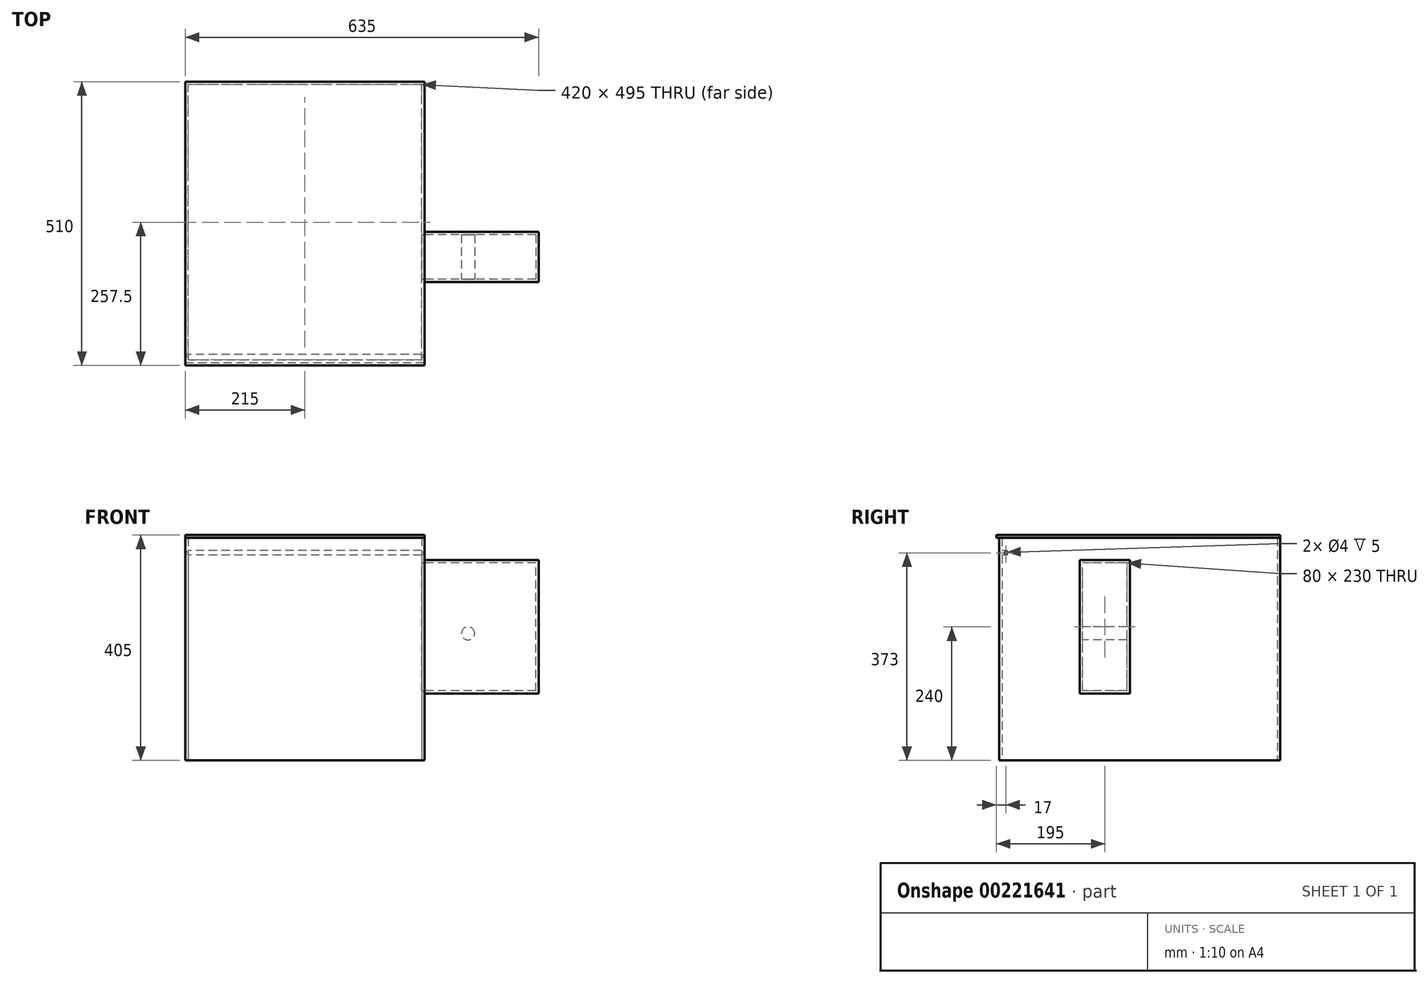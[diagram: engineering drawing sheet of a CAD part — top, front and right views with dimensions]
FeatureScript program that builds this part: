
annotation { "Feature Type Name" : "Feature", "Feature Type Description" : "" }
export const myFeature = defineFeature(function(context is Context, id is Id, definition is map)
    precondition{}
    {
        {
            var Q0;
            Q0=qCreatedBy(makeId("Top.planeOp"),FACE);
            var sketch = newSketch(context, id + "F0", { "sketchPlane" : qUnion([Q0])});
            skLineSegment(sketch, "E0.bottom", {"start": v(210, -250) * mm, "end": v(-210, -250) * mm});
            skLineSegment(sketch, "E0.top", {"start": v(210, 250) * mm, "end": v(-210, 250) * mm});
            skLineSegment(sketch, "E0.left", {"start": v(210, -250) * mm, "end": v(210, 250) * mm});
            skLineSegment(sketch, "E0.right", {"start": v(-210, -250) * mm, "end": v(-210, 250) * mm});
            skPoint(sketch, "E0.middle", {"position": v(0, 0) * mm});
            skLineSegment(sketch, "E1.0", {"start": v(-215, -250) * mm, "end": v(-215, 255) * mm});
            skLineSegment(sketch, "E1.1", {"start": v(215, 255) * mm, "end": v(-215, 255) * mm});
            skLineSegment(sketch, "E1.2", {"start": v(215, -250) * mm, "end": v(215, 255) * mm});
            skLineSegment(sketch, "E2", {"start": v(-215, -250) * mm, "end": v(-210, -250) * mm});
            skLineSegment(sketch, "E3", {"start": v(210, -250) * mm, "end": v(215, -250) * mm});
            skLineSegment(sketch, "E4", {"start": v(-210, -245) * mm, "end": v(210, -245) * mm});
            skSolve(sketch);
        }
        {
            var Q0;
            Q0=makeQuery(id+"F0.imprint","IMPRINT",FACE,{"disambiguationData":[TD([[makeQuery(id+"F0.imprint","IMPRINT",EDGE,{"derivedFrom":sQuery(id+"F0.wireOp",EDGE,"E0.top")}),-1.0]])]});
            extrude(context, id + "F1", {"entities" : qUnion([Q0]), "depth" : 400 * mm});
        }
        {
            var Q0;
            Q0=makeQuery(id+"F1.opExtrude","CAP_FACE",FACE,{"disambiguationData":[OSD([sQuery(id+"F0.wireOp",EDGE,"E0.top"),sQuery(id+"F0.wireOp",EDGE,"E0.left"),sQuery(id+"F0.wireOp",EDGE,"E0.right"),sQuery(id+"F0.wireOp",EDGE,"E1.0"),sQuery(id+"F0.wireOp",EDGE,"E1.1"),sQuery(id+"F0.wireOp",EDGE,"E1.2"),sQuery(id+"F0.wireOp",EDGE,"E2"),sQuery(id+"F0.wireOp",EDGE,"E3")])],"isStart":false});
            var sketch = newSketch(context, id + "F2", { "sketchPlane" : qUnion([Q0])});
            skLineSegment(sketch, "E5.bottom", {"start": v(215, 255) * mm, "end": v(-215, 255) * mm});
            skLineSegment(sketch, "E5.top", {"start": v(215, -255) * mm, "end": v(-215, -255) * mm});
            skLineSegment(sketch, "E5.left", {"start": v(215, 255) * mm, "end": v(215, -255) * mm});
            skLineSegment(sketch, "E5.right", {"start": v(-215, 255) * mm, "end": v(-215, -255) * mm});
            skPoint(sketch, "E5.middle", {"position": v(0, 0) * mm});
            skSolve(sketch);
        }
        {
            var Q0;
            {var subQ2=sQuery(id+"F2.wireOp",EDGE,"E5.top");Q0=makeQuery(id+"F2.imprint","IMPRINT",FACE,{"disambiguationData":[TD([[makeQuery(id+"F2.imprint","IMPRINT",EDGE,{"derivedFrom":subQ2}),-1.0]])]});}
            var Q1;
            {var subQ2=sQuery(id+"F2.wireOp",EDGE,"E5.bottom");Q1=makeQuery(id+"F2.imprint","IMPRINT",FACE,{"disambiguationData":[TD([[makeQuery(id+"F2.imprint","IMPRINT",EDGE,{"derivedFrom":subQ2}),1.0]])]});}
            extrude(context, id + "F3", {"entities" : qUnion([Q0, Q1]), "depth" : 5 * mm});
        }
        {
            var Q0;
            Q0=makeQuery(id+"F1.opExtrude","SWEPT_FACE",FACE,{"disambiguationData":[OSD([sQuery(id+"F0.wireOp",EDGE,"E1.0")])]});
            var sketch = newSketch(context, id + "F4", { "sketchPlane" : qUnion([Q0])});
            skCircle(sketch, "E6", {"center": v(238, 373) * mm, "radius": 2 * mm});
            skSolve(sketch);
        }
        {
            var Q0;
            Q0=makeQuery(id+"F4.imprint","IMPRINT",FACE,{"disambiguationData":[TD([[makeQuery(id+"F4.imprint","IMPRINT",EDGE,{"derivedFrom":sQuery(id+"F4.wireOp",EDGE,"E6")}),1.0]])]});
            extrude(context, id + "F5", {"entities" : qUnion([Q0]), "operationType" : NewBodyOperationType.REMOVE, "endBound" : BoundingType.UP_TO_NEXT, "oppositeDirection" : true, "depth" : 25 * mm});
        }
        {
            var Q0;
            Q0=makeQuery(id+"F1.opExtrude","SWEPT_FACE",FACE,{"disambiguationData":[OSD([sQuery(id+"F0.wireOp",EDGE,"E1.2")])]});
            var sketch = newSketch(context, id + "F6", { "sketchPlane" : qUnion([Q0])});
            skCircle(sketch, "E7", {"center": v(-238, 373) * mm, "radius": 2 * mm});
            skLineSegment(sketch, "E8.bottom", {"start": v(-20, 125) * mm, "end": v(-100, 125) * mm});
            skLineSegment(sketch, "E8.top", {"start": v(-20, 355) * mm, "end": v(-100, 355) * mm});
            skLineSegment(sketch, "E8.left", {"start": v(-20, 125) * mm, "end": v(-20, 355) * mm});
            skLineSegment(sketch, "E8.right", {"start": v(-100, 125) * mm, "end": v(-100, 355) * mm});
            skPoint(sketch, "E8.middle", {"position": v(-60, 240) * mm});
            skLineSegment(sketch, "E9.0", {"start": v(-105, 120) * mm, "end": v(-105, 360) * mm});
            skLineSegment(sketch, "E9.1", {"start": v(-15, 120) * mm, "end": v(-105, 120) * mm});
            skLineSegment(sketch, "E9.2", {"start": v(-15, 120) * mm, "end": v(-15, 360) * mm});
            skLineSegment(sketch, "E9.3", {"start": v(-15, 360) * mm, "end": v(-105, 360) * mm});
            skSolve(sketch);
        }
        {
            var Q0;
            Q0=makeQuery(id+"F6.imprint","IMPRINT",FACE,{"disambiguationData":[TD([[makeQuery(id+"F6.imprint","IMPRINT",EDGE,{"derivedFrom":sQuery(id+"F6.wireOp",EDGE,"E7")}),1.0]])]});
            extrude(context, id + "F7", {"entities" : qUnion([Q0]), "operationType" : NewBodyOperationType.REMOVE, "endBound" : BoundingType.UP_TO_NEXT, "oppositeDirection" : true, "depth" : 25 * mm});
        }
        {
            var Q0;
            Q0=makeQuery(id+"F6.imprint","IMPRINT",FACE,{"disambiguationData":[TD([[makeQuery(id+"F6.imprint","IMPRINT",EDGE,{"derivedFrom":sQuery(id+"F6.wireOp",EDGE,"E8.bottom")}),-1.0]])]});
            extrude(context, id + "F8", {"entities" : qUnion([Q0]), "operationType" : NewBodyOperationType.REMOVE, "endBound" : BoundingType.UP_TO_NEXT, "oppositeDirection" : true, "depth" : 25 * mm});
        }
        {
            var Q0;
            Q0=makeQuery(id+"F6.imprint","IMPRINT",FACE,{"disambiguationData":[TD([[makeQuery(id+"F6.imprint","IMPRINT",EDGE,{"derivedFrom":sQuery(id+"F6.wireOp",EDGE,"E8.bottom")}),1.0]])]});
            extrude(context, id + "F9", {"entities" : qUnion([Q0]), "depth" : 200 * mm});
        }
        {
            var Q0;
            Q0=makeQuery(id+"F9.opExtrude","CAP_FACE",FACE,{"disambiguationData":[OSD([sQuery(id+"F6.wireOp",EDGE,"E8.bottom"),sQuery(id+"F6.wireOp",EDGE,"E8.top"),sQuery(id+"F6.wireOp",EDGE,"E8.left"),sQuery(id+"F6.wireOp",EDGE,"E8.right"),sQuery(id+"F6.wireOp",EDGE,"E9.0"),sQuery(id+"F6.wireOp",EDGE,"E9.1"),sQuery(id+"F6.wireOp",EDGE,"E9.2"),sQuery(id+"F6.wireOp",EDGE,"E9.3")])],"isStart":false});
            var sketch = newSketch(context, id + "F10", { "sketchPlane" : qUnion([Q0])});
            skLineSegment(sketch, "E10.bottom", {"start": v(-105, 360) * mm, "end": v(-15, 360) * mm});
            skLineSegment(sketch, "E10.top", {"start": v(-105, 120) * mm, "end": v(-15, 120) * mm});
            skLineSegment(sketch, "E10.left", {"start": v(-105, 360) * mm, "end": v(-105, 120) * mm});
            skLineSegment(sketch, "E10.right", {"start": v(-15, 360) * mm, "end": v(-15, 120) * mm});
            skSolve(sketch);
        }
        {
            var Q0;
            Q0 = qSketchRegion(id + "F10", true);
            extrude(context, id + "F11", {"entities" : qUnion([Q0]), "operationType" : NewBodyOperationType.ADD, "depth" : 5 * mm});
        }
        {
            var Q0;
            Q0=makeQuery(id+"F11.boolean.opBoolean","MERGE",FACE,{"derivedFrom":[makeQuery(id+"F9.opExtrude","SWEPT_FACE",FACE,{"disambiguationData":[OSD([sQuery(id+"F6.wireOp",EDGE,"E9.0")])]}),makeQuery(id+"F11.opExtrude","SWEPT_FACE",FACE,{"disambiguationData":[OSD([sQuery(id+"F10.wireOp",EDGE,"E10.left")])]})]});
            var sketch = newSketch(context, id + "F12", { "sketchPlane" : qUnion([Q0])});
            skCircle(sketch, "E11", {"center": v(293.2, 228.2) * mm, "radius": 11.8 * mm});
            skSolve(sketch);
        }
        {
            var Q0;
            Q0=makeQuery(id+"F12.imprint","IMPRINT",FACE,{"disambiguationData":[TD([[makeQuery(id+"F12.imprint","IMPRINT",EDGE,{"derivedFrom":sQuery(id+"F12.wireOp",EDGE,"E11")}),1.0]])]});
            var Q1;
            Q1=makeQuery(id+"F9.opExtrude","SWEPT_FACE",FACE,{"disambiguationData":[OSD([sQuery(id+"F6.wireOp",EDGE,"E8.left")])]});
            extrude(context, id + "F13", {"entities" : qUnion([Q0]), "operationType" : NewBodyOperationType.ADD, "endBound" : BoundingType.UP_TO_SURFACE, "oppositeDirection" : true, "endBoundEntityFace" : qUnion([Q1]), "depth" : 25 * mm});
        }
        {
            var Q0;
            {var subQ0=sQuery(id+"F0.wireOp",EDGE,"E0.bottom");Q0=makeQuery(id+"F0.imprint","IMPRINT",FACE,{"disambiguationData":[TD([[makeQuery(id+"F0.imprint","IMPRINT",EDGE,{"derivedFrom":subQ0}),-1.0]])]});}
            extrude(context, id + "F14", {"entities" : qUnion([Q0]), "endBound" : BoundingType.UP_TO_NEXT, "depth" : 25 * mm});
        }
        {
            var Q0;
            Q0=makeQuery(id+"F14.opExtrude","SWEPT_FACE",FACE,{"disambiguationData":[OSD([sQuery(id+"F0.wireOp",EDGE,"E4")])]});
            var sketch = newSketch(context, id + "F15", { "sketchPlane" : qUnion([Q0])});
            skLineSegment(sketch, "E12.bottom", {"start": v(-210, 377.5) * mm, "end": v(210, 377.5) * mm});
            skLineSegment(sketch, "E12.top", {"start": v(-210, 368.76) * mm, "end": v(210, 368.76) * mm});
            skLineSegment(sketch, "E12.left", {"start": v(-210, 377.5) * mm, "end": v(-210, 368.76) * mm});
            skLineSegment(sketch, "E12.right", {"start": v(210, 377.5) * mm, "end": v(210, 368.76) * mm});
            skSolve(sketch);
        }
        {
            var Q0;
            Q0=makeQuery(id+"F15.imprint","IMPRINT",FACE,{"disambiguationData":[TD([[makeQuery(id+"F15.imprint","IMPRINT",EDGE,{"derivedFrom":sQuery(id+"F15.wireOp",EDGE,"E12.bottom")}),-1.0]])]});
            extrude(context, id + "F16", {"entities" : qUnion([Q0]), "operationType" : NewBodyOperationType.ADD, "depth" : 10 * mm});
        }
    });
